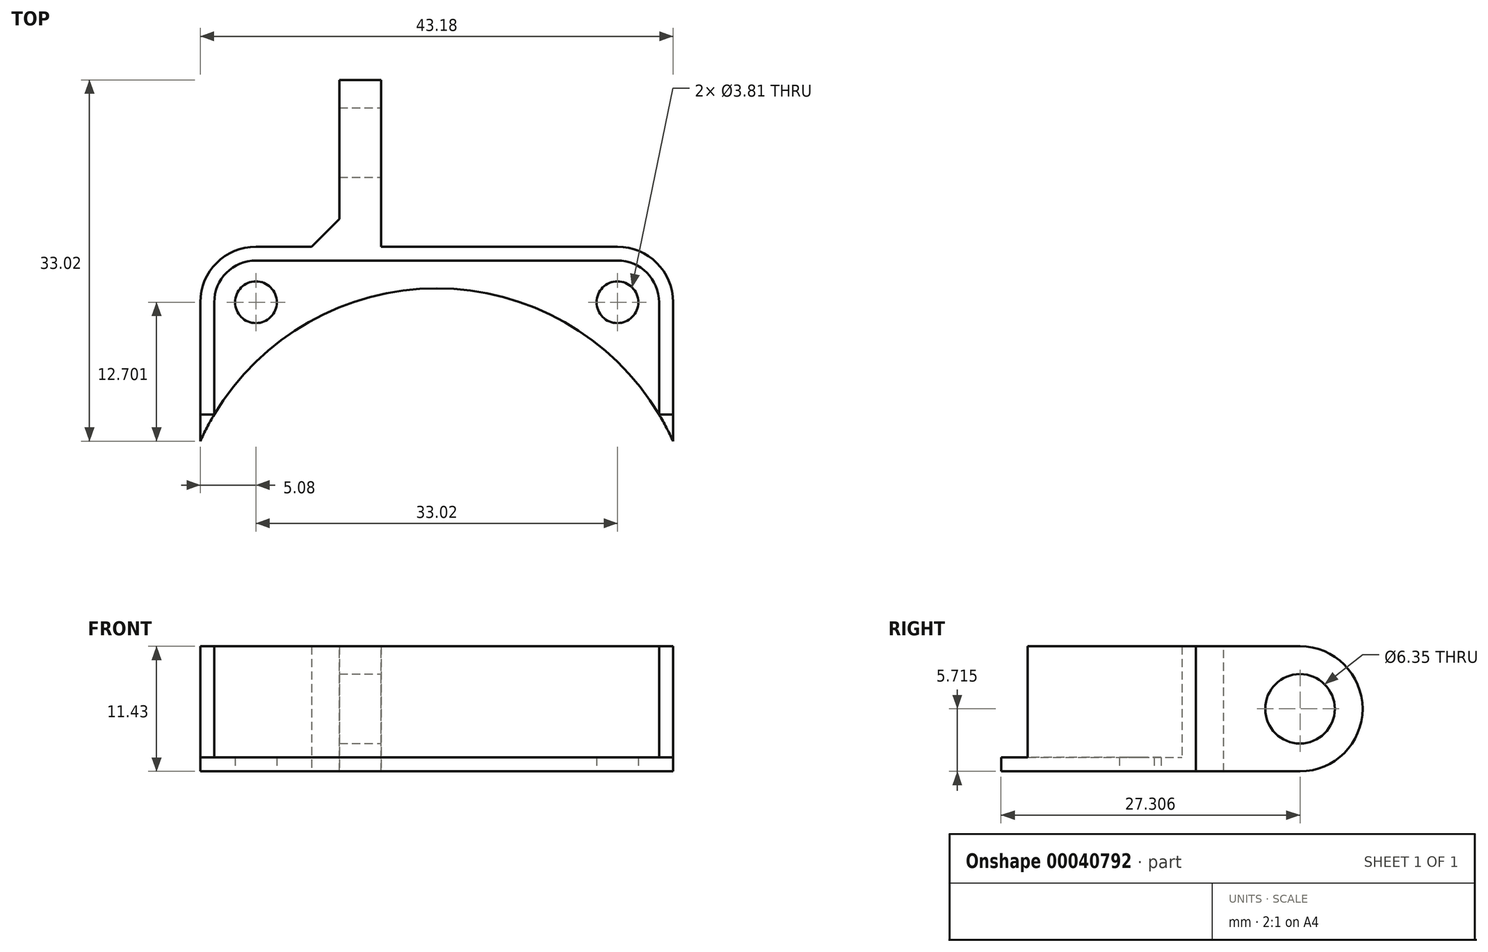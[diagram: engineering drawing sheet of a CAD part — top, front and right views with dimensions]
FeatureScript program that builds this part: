
annotation { "Feature Type Name" : "Feature", "Feature Type Description" : "" }
export const myFeature = defineFeature(function(context is Context, id is Id, definition is map)
    precondition{}
    {
        {
            var Q0;
            Q0=qCreatedBy(makeId("Top.planeOp"),FACE);
            var sketch = newSketch(context, id + "F0", { "sketchPlane" : qUnion([Q0])});
            skLineSegment(sketch, "E0.bottom", {"start": v(-16.51, 6.56) * mm, "end": v(16.51, 6.56) * mm});
            skLineSegment(sketch, "E0.left", {"start": v(-21.59, 1.48) * mm, "end": v(-21.59, -11.22) * mm});
            skLineSegment(sketch, "E0.right", {"start": v(21.59, 1.48) * mm, "end": v(21.59, -11.22) * mm});
            skPoint(sketch, "E1.visualSharp", {"position": v(21.59, 6.56) * mm});
            skArc(sketch, "E1.filletArc", {"start": v(21.59, 1.48) * mm, "mid": v(20.1, 5.07) * mm, "end": v(16.51, 6.56) * mm});
            skPoint(sketch, "E2.visualSharp", {"position": v(-21.59, 6.56) * mm});
            skArc(sketch, "E2.filletArc", {"start": v(-16.51, 6.56) * mm, "mid": v(-20.1, 5.07) * mm, "end": v(-21.59, 1.48) * mm});
            skArc(sketch, "E3", {"start": v(21.59, -11.22) * mm, "mid": v(0, 2.75) * mm, "end": v(-21.59, -11.22) * mm});
            skCircle(sketch, "E4", {"center": v(-16.51, 1.48) * mm, "radius": 1.9 * mm});
            skCircle(sketch, "E5", {"center": v(16.51, 1.48) * mm, "radius": 1.9 * mm});
            skLineSegment(sketch, "E6", {"start": v(-20.15, -8.5) * mm, "end": v(-21.59, -8.5) * mm});
            skPoint(sketch, "E6.endSnap0", {"position": v(-21.59, -4.87) * mm});
            skLineSegment(sketch, "E7", {"start": v(0, 0) * mm, "end": v(0, -11.06) * mm});
            skLineSegment(sketch, "E8.MirrorCS", {"start": v(20.15, -8.5) * mm, "end": v(21.59, -8.5) * mm});
            skSolve(sketch);
        }
        {
            var Q0;
            Q0 = qSketchRegion(id + "F0", true);
            extrude(context, id + "F1", {"entities" : qUnion([Q0]), "depth" : 1.27 * mm, "offsetDistance" : 25.4 * mm});
        }
        {
            var Q0;
            Q0=makeQuery(id+"F1.opExtrude","CAP_FACE",FACE,{"disambiguationData":[OSD([sQuery(id+"F0.wireOp",EDGE,"E0.bottom"),sQuery(id+"F0.wireOp",EDGE,"E0.left"),sQuery(id+"F0.wireOp",EDGE,"E0.right"),sQuery(id+"F0.wireOp",EDGE,"E1.filletArc"),sQuery(id+"F0.wireOp",EDGE,"E2.filletArc"),sQuery(id+"F0.wireOp",EDGE,"E3"),sQuery(id+"F0.wireOp",EDGE,"E4"),sQuery(id+"F0.wireOp",EDGE,"E5")])],"isStart":false});
            var sketch = newSketch(context, id + "F2", { "sketchPlane" : qUnion([Q0])});
            skLineSegment(sketch, "E9.0", {"start": v(21.59, 1.48) * mm, "end": v(21.59, -11.22) * mm});
            skArc(sketch, "E9.1", {"start": v(21.59, 1.48) * mm, "mid": v(20.1, 5.07) * mm, "end": v(16.51, 6.56) * mm});
            skLineSegment(sketch, "E9.2", {"start": v(-16.51, 6.56) * mm, "end": v(16.51, 6.56) * mm});
            skArc(sketch, "E9.3", {"start": v(-16.51, 6.56) * mm, "mid": v(-20.1, 5.07) * mm, "end": v(-21.59, 1.48) * mm});
            skLineSegment(sketch, "E9.4", {"start": v(-21.59, 1.48) * mm, "end": v(-21.59, -11.22) * mm});
            skArc(sketch, "E9.5", {"start": v(21.59, -11.22) * mm, "mid": v(0, 2.75) * mm, "end": v(-21.59, -11.22) * mm});
            skLineSegment(sketch, "E10.0", {"start": v(20.32, 1.48) * mm, "end": v(20.32, -8.78) * mm});
            skLineSegment(sketch, "E10.1", {"start": v(-16.51, 5.3) * mm, "end": v(16.51, 5.3) * mm});
            skLineSegment(sketch, "E10.2", {"start": v(-20.32, 1.48) * mm, "end": v(-20.32, -8.78) * mm});
            skPoint(sketch, "E11.visualSharp", {"position": v(-20.32, 5.3) * mm});
            skArc(sketch, "E11.filletArc", {"start": v(-16.51, 5.3) * mm, "mid": v(-19.2, 4.18) * mm, "end": v(-20.32, 1.48) * mm});
            skPoint(sketch, "E12.visualSharp", {"position": v(20.32, 5.3) * mm});
            skArc(sketch, "E12.filletArc", {"start": v(20.32, 1.48) * mm, "mid": v(19.2, 4.18) * mm, "end": v(16.51, 5.3) * mm});
            skLineSegment(sketch, "E13", {"start": v(-20.32, -8.78) * mm, "end": v(-21.59, -8.78) * mm});
            skLineSegment(sketch, "E14", {"start": v(20.32, -8.78) * mm, "end": v(21.59, -8.78) * mm});
            skSolve(sketch);
        }
        {
            var Q0;
            {var subQ3=sQuery(id+"F2.wireOp",EDGE,"E9.1");Q0=makeQuery(id+"F2.imprint","IMPRINT",FACE,{"disambiguationData":[TD([[makeQuery(id+"F2.imprint","IMPRINT",EDGE,{"derivedFrom":subQ3}),1.0]])]});}
            extrude(context, id + "F3", {"entities" : qUnion([Q0]), "operationType" : NewBodyOperationType.ADD, "depth" : 10.16 * mm, "offsetDistance" : 25.4 * mm});
        }
        {
            var Q0;
            Q0=makeQuery(id+"F3.boolean.opBoolean","MERGE",FACE,{"derivedFrom":[makeQuery(id+"F1.opExtrude","SWEPT_FACE",FACE,{"disambiguationData":[OSD([sQuery(id+"F0.wireOp",EDGE,"E0.bottom")])]}),makeQuery(id+"F3.opExtrude","SWEPT_FACE",FACE,{"disambiguationData":[OSD([sQuery(id+"F2.wireOp",EDGE,"E9.2")])]})]});
            var sketch = newSketch(context, id + "F4", { "sketchPlane" : qUnion([Q0])});
            skLineSegment(sketch, "E15", {"start": v(5.08, 11.43) * mm, "end": v(5.08, 0) * mm});
            skLineSegment(sketch, "E16", {"start": v(8.9, 11.43) * mm, "end": v(8.9, 0) * mm});
            skSolve(sketch);
        }
        {
            var Q0;
            {var subQ0=sQuery(id+"F4.wireOp",EDGE,"E15");Q0=makeQuery(id+"F4.imprint","IMPRINT",FACE,{"disambiguationData":[TD([[makeQuery(id+"F4.imprint","IMPRINT",EDGE,{"derivedFrom":subQ0}),1.0]])]});}
            extrude(context, id + "F5", {"entities" : qUnion([Q0]), "operationType" : NewBodyOperationType.ADD, "depth" : 15.24 * mm, "offsetDistance" : 25.4 * mm});
        }
        {
            var Q0;
            Q0=makeQuery(id+"F5.opExtrude","SWEPT_FACE",FACE,{"disambiguationData":[OSD([sQuery(id+"F4.wireOp",EDGE,"E15")])]});
            var sketch = newSketch(context, id + "F6", { "sketchPlane" : qUnion([Q0])});
            skArc(sketch, "E17", {"start": v(16.09, 0) * mm, "mid": v(21.8, 5.72) * mm, "end": v(16.09, 11.43) * mm});
            skPoint(sketch, "E17.centerSnap0", {"position": v(21.8, 5.72) * mm});
            skLineSegment(sketch, "E18", {"start": v(16.09, 11.43) * mm, "end": v(21.8, 11.43) * mm});
            skLineSegment(sketch, "E19", {"start": v(21.8, 11.43) * mm, "end": v(21.8, 5.72) * mm});
            skLineSegment(sketch, "E20", {"start": v(21.8, 5.72) * mm, "end": v(21.8, 0) * mm});
            skLineSegment(sketch, "E21", {"start": v(21.8, 0) * mm, "end": v(16.09, 0) * mm});
            skCircle(sketch, "E22", {"center": v(16.09, 5.72) * mm, "radius": 3.18 * mm});
            skSolve(sketch);
        }
        {
            var Q0;
            {var subQ2=sQuery(id+"F6.wireOp",EDGE,"E20");Q0=makeQuery(id+"F6.imprint","IMPRINT",FACE,{"disambiguationData":[TD([[makeQuery(id+"F6.imprint","IMPRINT",EDGE,{"derivedFrom":subQ2}),-1.0]])]});}
            var Q1;
            Q1=makeQuery(id+"F6.imprint","IMPRINT",FACE,{"disambiguationData":[TD([[makeQuery(id+"F6.imprint","IMPRINT",EDGE,{"derivedFrom":sQuery(id+"F6.wireOp",EDGE,"E22")}),1.0]])]});
            var Q2;
            {var subQ0=sQuery(id+"F6.wireOp",EDGE,"E18");Q2=makeQuery(id+"F6.imprint","IMPRINT",FACE,{"disambiguationData":[TD([[makeQuery(id+"F6.imprint","IMPRINT",EDGE,{"derivedFrom":subQ0}),1.0]])]});}
            extrude(context, id + "F7", {"entities" : qUnion([Q0, Q1, Q2]), "operationType" : NewBodyOperationType.REMOVE, "oppositeDirection" : true, "depth" : 25.4 * mm, "offsetDistance" : 25.4 * mm});
        }
        {
            var Q0;
            Q0=makeQuery(id+"F5.opExtrude","CAP_EDGE",EDGE,{"disambiguationData":[OSD([sQuery(id+"F4.wireOp",EDGE,"E15")])],"isStart":true});
            var Q1;
            Q1=makeQuery(id+"F5.opExtrude","CAP_EDGE",EDGE,{"disambiguationData":[OSD([sQuery(id+"F4.wireOp",EDGE,"E16")])],"isStart":true});
            chamfer(context, id + "F8", {"entities" : qUnion([Q0, Q1]), "width" : 2.54 * mm, "tangentPropagation" : true});
        }
    });
